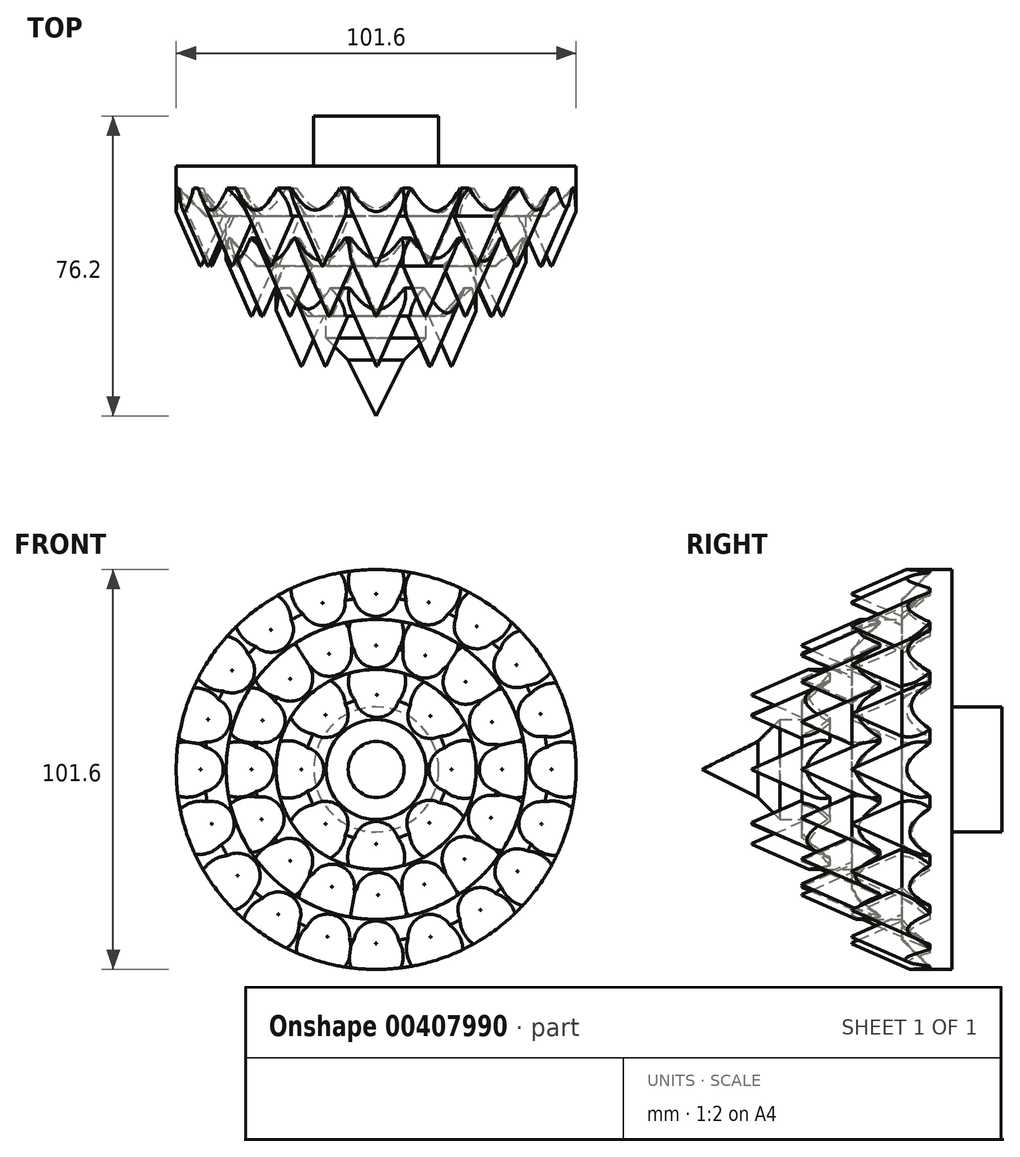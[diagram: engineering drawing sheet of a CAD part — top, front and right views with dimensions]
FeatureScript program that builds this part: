
annotation { "Feature Type Name" : "Feature", "Feature Type Description" : "" }
export const myFeature = defineFeature(function(context is Context, id is Id, definition is map)
    precondition{}
    {
        {
            var Q0;
            Q0=qCreatedBy(makeId("Front.planeOp"),FACE);
            var sketch = newSketch(context, id + "F0", { "sketchPlane" : qUnion([Q0])});
            skCircle(sketch, "E0", {"center": v(0, 0) * mm, "radius": 15.88 * mm});
            skSolve(sketch);
        }
        {
            var Q0;
            Q0 = qSketchRegion(id + "F0", true);
            extrude(context, id + "F1", {"entities" : qUnion([Q0]), "depth" : 12.7 * mm});
        }
        {
            var Q0;
            Q0=makeQuery(id+"F1.opExtrude","CAP_FACE",FACE,{"disambiguationData":[OSD([sQuery(id+"F0.wireOp",EDGE,"E0")])],"isStart":false});
            var sketch = newSketch(context, id + "F2", { "sketchPlane" : qUnion([Q0])});
            skCircle(sketch, "E1", {"center": v(0, 0) * mm, "radius": 50.8 * mm});
            skSolve(sketch);
        }
        {
            var Q0;
            Q0 = qSketchRegion(id + "F2", true);
            extrude(context, id + "F3", {"entities" : qUnion([Q0]), "operationType" : NewBodyOperationType.ADD, "depth" : 12.7 * mm});
        }
        {
            var Q0;
            Q0=makeQuery(id+"F3.opExtrude","CAP_FACE",FACE,{"disambiguationData":[OSD([sQuery(id+"F2.wireOp",EDGE,"E1")])],"isStart":false});
            var sketch = newSketch(context, id + "F4", { "sketchPlane" : qUnion([Q0])});
            skCircle(sketch, "E2", {"center": v(0, 0) * mm, "radius": 38.1 * mm});
            skSolve(sketch);
        }
        {
            var Q0;
            Q0 = qSketchRegion(id + "F4", true);
            extrude(context, id + "F5", {"entities" : qUnion([Q0]), "operationType" : NewBodyOperationType.ADD, "depth" : 12.7 * mm});
        }
        {
            var Q0;
            Q0=makeQuery(id+"F5.opExtrude","CAP_FACE",FACE,{"disambiguationData":[OSD([sQuery(id+"F4.wireOp",EDGE,"E2")])],"isStart":false});
            var sketch = newSketch(context, id + "F6", { "sketchPlane" : qUnion([Q0])});
            skCircle(sketch, "E3", {"center": v(0, 0) * mm, "radius": 25.4 * mm});
            skSolve(sketch);
        }
        {
            var Q0;
            Q0 = qSketchRegion(id + "F6", true);
            extrude(context, id + "F7", {"entities" : qUnion([Q0]), "operationType" : NewBodyOperationType.ADD, "depth" : 12.7 * mm});
        }
        {
            var Q0;
            Q0=makeQuery(id+"F7.opExtrude","CAP_FACE",FACE,{"disambiguationData":[OSD([sQuery(id+"F6.wireOp",EDGE,"E3")])],"isStart":false});
            var sketch = newSketch(context, id + "F8", { "sketchPlane" : qUnion([Q0])});
            skCircle(sketch, "E4", {"center": v(0, 0) * mm, "radius": 12.7 * mm});
            skSolve(sketch);
        }
        {
            var Q0;
            Q0 = qSketchRegion(id + "F8", true);
            extrude(context, id + "F9", {"entities" : qUnion([Q0]), "operationType" : NewBodyOperationType.ADD, "depth" : 12.7 * mm});
        }
        {
            var Q0;
            Q0=makeQuery(id+"F9.opExtrude","CAP_FACE",FACE,{"disambiguationData":[OSD([sQuery(id+"F8.wireOp",EDGE,"E4")])],"isStart":false});
            var sketch = newSketch(context, id + "F10", { "sketchPlane" : qUnion([Q0])});
            skCircle(sketch, "E5", {"center": v(0, 0) * mm, "radius": 6.35 * mm});
            skSolve(sketch);
        }
        {
            var Q0;
            Q0 = qSketchRegion(id + "F10", true);
            extrude(context, id + "F11", {"entities" : qUnion([Q0]), "operationType" : NewBodyOperationType.ADD, "depth" : 12.7 * mm});
        }
        {
            var Q0;
            Q0=makeQuery(id+"F11.opExtrude","CAP_EDGE",EDGE,{"disambiguationData":[OSD([sQuery(id+"F10.wireOp",EDGE,"E5")])],"isStart":false});
            chamfer(context, id + "F12", {"entities" : qUnion([Q0]), "chamferType" : ChamferType.TWO_OFFSETS, "width1" : 6.35 * mm, "oppositeDirection" : false, "width2" : 12.7 * mm, "tangentPropagation" : true});
        }
        {
            var Q0;
            Q0=makeQuery(id+"F3.opExtrude","CAP_FACE",FACE,{"disambiguationData":[OSD([sQuery(id+"F2.wireOp",EDGE,"E1")])],"isStart":false});
            var sketch = newSketch(context, id + "F13", { "sketchPlane" : qUnion([Q0])});
            skCircle(sketch, "E6", {"center": v(25.56, 36.37) * mm, "radius": 5.72 * mm});
            skCircle(sketch, "E7", {"center": v(35.65, 26.5) * mm, "radius": 5.72 * mm});
            skCircle(sketch, "E8", {"center": v(41.76, 14.06) * mm, "radius": 5.72 * mm});
            skCircle(sketch, "E9", {"center": v(44.58, 0) * mm, "radius": 5.72 * mm});
            skCircle(sketch, "E10", {"center": v(42, -13.89) * mm, "radius": 5.72 * mm});
            skCircle(sketch, "E11", {"center": v(35.89, -25.86) * mm, "radius": 5.72 * mm});
            skCircle(sketch, "E12", {"center": v(26.5, -35.73) * mm, "radius": 5.72 * mm});
            skCircle(sketch, "E13", {"center": v(13.34, 42.47) * mm, "radius": 5.72 * mm});
            skCircle(sketch, "E14", {"center": v(0, 44.59) * mm, "radius": 5.72 * mm});
            skCircle(sketch, "E15", {"center": v(0, -44.18) * mm, "radius": 5.72 * mm});
            skCircle(sketch, "E16", {"center": v(13.81, -42.54) * mm, "radius": 5.72 * mm});
            skCircle(sketch, "E17", {"center": v(-12.4, -42.47) * mm, "radius": 5.72 * mm});
            skCircle(sketch, "E18", {"center": v(-24.85, -36.84) * mm, "radius": 5.72 * mm});
            skCircle(sketch, "E19", {"center": v(-35.18, -26.98) * mm, "radius": 5.72 * mm});
            skCircle(sketch, "E20", {"center": v(-41.76, -13.82) * mm, "radius": 5.72 * mm});
            skCircle(sketch, "E21", {"center": v(-44.58, 0) * mm, "radius": 5.72 * mm});
            skCircle(sketch, "E22", {"center": v(-42.7, 12.71) * mm, "radius": 5.72 * mm});
            skCircle(sketch, "E23", {"center": v(-36.6, 25.16) * mm, "radius": 5.72 * mm});
            skCircle(sketch, "E24", {"center": v(-26.73, 35.5) * mm, "radius": 5.72 * mm});
            skCircle(sketch, "E25", {"center": v(-13.58, 42.3) * mm, "radius": 5.72 * mm});
            skSolve(sketch);
        }
        {
            var Q0;
            Q0 = qSketchRegion(id + "F13", true);
            extrude(context, id + "F14", {"entities" : qUnion([Q0]), "operationType" : NewBodyOperationType.ADD, "depth" : 12.7 * mm});
        }
        {
            var Q0;
            Q0=makeQuery(id+"F14.opExtrude","CAP_EDGE",EDGE,{"disambiguationData":[OSD([sQuery(id+"F13.wireOp",EDGE,"E20")])],"isStart":false});
            var Q1;
            Q1=makeQuery(id+"F14.opExtrude","CAP_EDGE",EDGE,{"disambiguationData":[OSD([sQuery(id+"F13.wireOp",EDGE,"E21")])],"isStart":false});
            var Q2;
            Q2=makeQuery(id+"F14.opExtrude","CAP_EDGE",EDGE,{"disambiguationData":[OSD([sQuery(id+"F13.wireOp",EDGE,"E22")])],"isStart":false});
            var Q3;
            Q3=makeQuery(id+"F14.opExtrude","CAP_EDGE",EDGE,{"disambiguationData":[OSD([sQuery(id+"F13.wireOp",EDGE,"E23")])],"isStart":false});
            var Q4;
            Q4=makeQuery(id+"F14.opExtrude","CAP_EDGE",EDGE,{"disambiguationData":[OSD([sQuery(id+"F13.wireOp",EDGE,"E24")])],"isStart":false});
            var Q5;
            Q5=makeQuery(id+"F14.opExtrude","CAP_EDGE",EDGE,{"disambiguationData":[OSD([sQuery(id+"F13.wireOp",EDGE,"E25")])],"isStart":false});
            var Q6;
            Q6=makeQuery(id+"F14.opExtrude","CAP_EDGE",EDGE,{"disambiguationData":[OSD([sQuery(id+"F13.wireOp",EDGE,"E14")])],"isStart":false});
            var Q7;
            Q7=makeQuery(id+"F14.opExtrude","CAP_EDGE",EDGE,{"disambiguationData":[OSD([sQuery(id+"F13.wireOp",EDGE,"E13")])],"isStart":false});
            var Q8;
            Q8=makeQuery(id+"F14.opExtrude","CAP_EDGE",EDGE,{"disambiguationData":[OSD([sQuery(id+"F13.wireOp",EDGE,"E6")])],"isStart":false});
            var Q9;
            Q9=makeQuery(id+"F14.opExtrude","CAP_EDGE",EDGE,{"disambiguationData":[OSD([sQuery(id+"F13.wireOp",EDGE,"E7")])],"isStart":false});
            var Q10;
            Q10=makeQuery(id+"F14.opExtrude","CAP_EDGE",EDGE,{"disambiguationData":[OSD([sQuery(id+"F13.wireOp",EDGE,"E8")])],"isStart":false});
            var Q11;
            Q11=makeQuery(id+"F14.opExtrude","CAP_EDGE",EDGE,{"disambiguationData":[OSD([sQuery(id+"F13.wireOp",EDGE,"E9")])],"isStart":false});
            var Q12;
            Q12=makeQuery(id+"F14.opExtrude","CAP_EDGE",EDGE,{"disambiguationData":[OSD([sQuery(id+"F13.wireOp",EDGE,"E10")])],"isStart":false});
            var Q13;
            Q13=makeQuery(id+"F14.opExtrude","CAP_EDGE",EDGE,{"disambiguationData":[OSD([sQuery(id+"F13.wireOp",EDGE,"E11")])],"isStart":false});
            var Q14;
            Q14=makeQuery(id+"F14.opExtrude","CAP_EDGE",EDGE,{"disambiguationData":[OSD([sQuery(id+"F13.wireOp",EDGE,"E12")])],"isStart":false});
            var Q15;
            Q15=makeQuery(id+"F14.opExtrude","CAP_EDGE",EDGE,{"disambiguationData":[OSD([sQuery(id+"F13.wireOp",EDGE,"E16")])],"isStart":false});
            var Q16;
            Q16=makeQuery(id+"F14.opExtrude","CAP_EDGE",EDGE,{"disambiguationData":[OSD([sQuery(id+"F13.wireOp",EDGE,"E15")])],"isStart":false});
            var Q17;
            Q17=makeQuery(id+"F14.opExtrude","CAP_EDGE",EDGE,{"disambiguationData":[OSD([sQuery(id+"F13.wireOp",EDGE,"E17")])],"isStart":false});
            var Q18;
            Q18=makeQuery(id+"F14.opExtrude","CAP_EDGE",EDGE,{"disambiguationData":[OSD([sQuery(id+"F13.wireOp",EDGE,"E18")])],"isStart":false});
            var Q19;
            Q19=makeQuery(id+"F14.opExtrude","CAP_EDGE",EDGE,{"disambiguationData":[OSD([sQuery(id+"F13.wireOp",EDGE,"E19")])],"isStart":false});
            chamfer(context, id + "F15", {"entities" : qUnion([Q0, Q1, Q2, Q3, Q4, Q5, Q6, Q7, Q8, Q9, Q10, Q11, Q12, Q13, Q14, Q15, Q16, Q17, Q18, Q19]), "chamferType" : ChamferType.TWO_OFFSETS, "width1" : 5.6 * mm, "oppositeDirection" : false, "width2" : 12.7 * mm, "tangentPropagation" : true});
        }
        {
            var Q0;
            Q0=makeQuery(id+"F5.opExtrude","CAP_FACE",FACE,{"disambiguationData":[OSD([sQuery(id+"F4.wireOp",EDGE,"E2")])],"isStart":false});
            var sketch = newSketch(context, id + "F16", { "sketchPlane" : qUnion([Q0])});
            skCircle(sketch, "E26", {"center": v(-31.68, 0) * mm, "radius": 5.72 * mm});
            skCircle(sketch, "E27", {"center": v(0, 31.5) * mm, "radius": 5.72 * mm});
            skCircle(sketch, "E28", {"center": v(0.51, -31.9) * mm, "radius": 5.72 * mm});
            skCircle(sketch, "E29", {"center": v(31.95, 0) * mm, "radius": 5.72 * mm});
            skCircle(sketch, "E30", {"center": v(29.39, 12.04) * mm, "radius": 5.72 * mm});
            skCircle(sketch, "E31", {"center": v(22.73, 22.29) * mm, "radius": 5.72 * mm});
            skCircle(sketch, "E32", {"center": v(12.48, 28.95) * mm, "radius": 5.72 * mm});
            skCircle(sketch, "E33", {"center": v(29.13, -12.29) * mm, "radius": 5.72 * mm});
            skCircle(sketch, "E34", {"center": v(22.47, -22.79) * mm, "radius": 5.72 * mm});
            skCircle(sketch, "E35", {"center": v(12.23, -29.19) * mm, "radius": 5.72 * mm});
            skCircle(sketch, "E36", {"center": v(-11.25, -29.8) * mm, "radius": 5.72 * mm});
            skCircle(sketch, "E37", {"center": v(-21.82, -23.22) * mm, "radius": 5.72 * mm});
            skCircle(sketch, "E38", {"center": v(-29.1, -12.65) * mm, "radius": 5.72 * mm});
            skCircle(sketch, "E39", {"center": v(-28.86, 12.48) * mm, "radius": 5.72 * mm});
            skCircle(sketch, "E40", {"center": v(-21.82, 23.05) * mm, "radius": 5.72 * mm});
            skCircle(sketch, "E41", {"center": v(-11.96, 29.39) * mm, "radius": 5.72 * mm});
            skSolve(sketch);
        }
        {
            var Q0;
            Q0 = qSketchRegion(id + "F16", true);
            extrude(context, id + "F17", {"entities" : qUnion([Q0]), "operationType" : NewBodyOperationType.ADD, "depth" : 12.7 * mm});
        }
        {
            var Q0;
            Q0=makeQuery(id+"F17.opExtrude","CAP_EDGE",EDGE,{"disambiguationData":[OSD([sQuery(id+"F16.wireOp",EDGE,"E33")])],"isStart":false});
            var Q1;
            Q1=makeQuery(id+"F17.opExtrude","CAP_EDGE",EDGE,{"disambiguationData":[OSD([sQuery(id+"F16.wireOp",EDGE,"E29")])],"isStart":false});
            var Q2;
            Q2=makeQuery(id+"F17.opExtrude","CAP_EDGE",EDGE,{"disambiguationData":[OSD([sQuery(id+"F16.wireOp",EDGE,"E30")])],"isStart":false});
            var Q3;
            Q3=makeQuery(id+"F17.opExtrude","CAP_EDGE",EDGE,{"disambiguationData":[OSD([sQuery(id+"F16.wireOp",EDGE,"E31")])],"isStart":false});
            var Q4;
            Q4=makeQuery(id+"F17.opExtrude","CAP_EDGE",EDGE,{"disambiguationData":[OSD([sQuery(id+"F16.wireOp",EDGE,"E32")])],"isStart":false});
            var Q5;
            Q5=makeQuery(id+"F17.opExtrude","CAP_EDGE",EDGE,{"disambiguationData":[OSD([sQuery(id+"F16.wireOp",EDGE,"E27")])],"isStart":false});
            var Q6;
            Q6=makeQuery(id+"F17.opExtrude","CAP_EDGE",EDGE,{"disambiguationData":[OSD([sQuery(id+"F16.wireOp",EDGE,"E41")])],"isStart":false});
            var Q7;
            Q7=makeQuery(id+"F17.opExtrude","CAP_EDGE",EDGE,{"disambiguationData":[OSD([sQuery(id+"F16.wireOp",EDGE,"E40")])],"isStart":false});
            var Q8;
            Q8=makeQuery(id+"F17.opExtrude","CAP_EDGE",EDGE,{"disambiguationData":[OSD([sQuery(id+"F16.wireOp",EDGE,"E39")])],"isStart":false});
            var Q9;
            Q9=makeQuery(id+"F17.opExtrude","CAP_EDGE",EDGE,{"disambiguationData":[OSD([sQuery(id+"F16.wireOp",EDGE,"E26")])],"isStart":false});
            var Q10;
            Q10=makeQuery(id+"F17.opExtrude","CAP_EDGE",EDGE,{"disambiguationData":[OSD([sQuery(id+"F16.wireOp",EDGE,"E38")])],"isStart":false});
            var Q11;
            Q11=makeQuery(id+"F17.opExtrude","CAP_EDGE",EDGE,{"disambiguationData":[OSD([sQuery(id+"F16.wireOp",EDGE,"E37")])],"isStart":false});
            var Q12;
            Q12=makeQuery(id+"F17.opExtrude","CAP_EDGE",EDGE,{"disambiguationData":[OSD([sQuery(id+"F16.wireOp",EDGE,"E36")])],"isStart":false});
            var Q13;
            Q13=makeQuery(id+"F17.opExtrude","CAP_EDGE",EDGE,{"disambiguationData":[OSD([sQuery(id+"F16.wireOp",EDGE,"E28")])],"isStart":false});
            var Q14;
            Q14=makeQuery(id+"F17.opExtrude","CAP_EDGE",EDGE,{"disambiguationData":[OSD([sQuery(id+"F16.wireOp",EDGE,"E35")])],"isStart":false});
            var Q15;
            Q15=makeQuery(id+"F17.opExtrude","CAP_EDGE",EDGE,{"disambiguationData":[OSD([sQuery(id+"F16.wireOp",EDGE,"E34")])],"isStart":false});
            chamfer(context, id + "F18", {"entities" : qUnion([Q0, Q1, Q2, Q3, Q4, Q5, Q6, Q7, Q8, Q9, Q10, Q11, Q12, Q13, Q14, Q15]), "chamferType" : ChamferType.TWO_OFFSETS, "width1" : 5.6 * mm, "oppositeDirection" : false, "width2" : 12.7 * mm, "tangentPropagation" : true});
        }
        {
            var Q0;
            Q0=makeQuery(id+"F7.opExtrude","CAP_FACE",FACE,{"disambiguationData":[OSD([sQuery(id+"F6.wireOp",EDGE,"E3")])],"isStart":false});
            var sketch = newSketch(context, id + "F19", { "sketchPlane" : qUnion([Q0])});
            skCircle(sketch, "E42", {"center": v(-19.02, 0) * mm, "radius": 5.72 * mm});
            skCircle(sketch, "E43", {"center": v(0.2, 18.96) * mm, "radius": 5.72 * mm});
            skCircle(sketch, "E44", {"center": v(19.14, 0) * mm, "radius": 5.72 * mm});
            skCircle(sketch, "E45", {"center": v(0, -18.94) * mm, "radius": 5.72 * mm});
            skCircle(sketch, "E46", {"center": v(-12.87, -13.82) * mm, "radius": 5.72 * mm});
            skCircle(sketch, "E47", {"center": v(-12.87, 13.84) * mm, "radius": 5.72 * mm});
            skCircle(sketch, "E48", {"center": v(13.77, 13.58) * mm, "radius": 5.72 * mm});
            skCircle(sketch, "E49", {"center": v(13.5, -13.57) * mm, "radius": 5.72 * mm});
            skSolve(sketch);
        }
        {
            var Q0;
            Q0 = qSketchRegion(id + "F19", true);
            extrude(context, id + "F20", {"entities" : qUnion([Q0]), "operationType" : NewBodyOperationType.ADD, "depth" : 12.7 * mm});
        }
        {
            var Q0;
            Q0=makeQuery(id+"F20.opExtrude","CAP_EDGE",EDGE,{"disambiguationData":[OSD([sQuery(id+"F19.wireOp",EDGE,"E45")])],"isStart":false});
            var Q1;
            Q1=makeQuery(id+"F20.opExtrude","CAP_EDGE",EDGE,{"disambiguationData":[OSD([sQuery(id+"F19.wireOp",EDGE,"E46")])],"isStart":false});
            var Q2;
            Q2=makeQuery(id+"F20.opExtrude","CAP_EDGE",EDGE,{"disambiguationData":[OSD([sQuery(id+"F19.wireOp",EDGE,"E42")])],"isStart":false});
            var Q3;
            Q3=makeQuery(id+"F20.opExtrude","CAP_EDGE",EDGE,{"disambiguationData":[OSD([sQuery(id+"F19.wireOp",EDGE,"E47")])],"isStart":false});
            var Q4;
            Q4=makeQuery(id+"F20.opExtrude","CAP_EDGE",EDGE,{"disambiguationData":[OSD([sQuery(id+"F19.wireOp",EDGE,"E43")])],"isStart":false});
            var Q5;
            Q5=makeQuery(id+"F20.opExtrude","CAP_EDGE",EDGE,{"disambiguationData":[OSD([sQuery(id+"F19.wireOp",EDGE,"E48")])],"isStart":false});
            var Q6;
            Q6=makeQuery(id+"F20.opExtrude","CAP_EDGE",EDGE,{"disambiguationData":[OSD([sQuery(id+"F19.wireOp",EDGE,"E44")])],"isStart":false});
            var Q7;
            Q7=makeQuery(id+"F20.opExtrude","CAP_EDGE",EDGE,{"disambiguationData":[OSD([sQuery(id+"F19.wireOp",EDGE,"E49")])],"isStart":false});
            chamfer(context, id + "F21", {"entities" : qUnion([Q0, Q1, Q2, Q3, Q4, Q5, Q6, Q7]), "chamferType" : ChamferType.TWO_OFFSETS, "width1" : 5.6 * mm, "oppositeDirection" : false, "width2" : 12.7 * mm, "tangentPropagation" : true});
        }
        {
            var Q0;
            Q0=makeQuery(id+"F3.opExtrude","CAP_EDGE",EDGE,{"disambiguationData":[OSD([sQuery(id+"F2.wireOp",EDGE,"E1")])],"isStart":false});
            var Q1;
            Q1=makeQuery(id+"F5.opExtrude","CAP_EDGE",EDGE,{"disambiguationData":[OSD([sQuery(id+"F4.wireOp",EDGE,"E2")])],"isStart":false});
            var Q2;
            Q2=makeQuery(id+"F7.opExtrude","CAP_EDGE",EDGE,{"disambiguationData":[OSD([sQuery(id+"F6.wireOp",EDGE,"E3")])],"isStart":false});
            var Q3;
            Q3=makeQuery(id+"F9.opExtrude","CAP_EDGE",EDGE,{"disambiguationData":[OSD([sQuery(id+"F8.wireOp",EDGE,"E4")])],"isStart":false});
            chamfer(context, id + "F22", {"entities" : qUnion([Q0, Q1, Q2, Q3]), "width" : 7.11 * mm, "tangentPropagation" : true});
        }
    });
